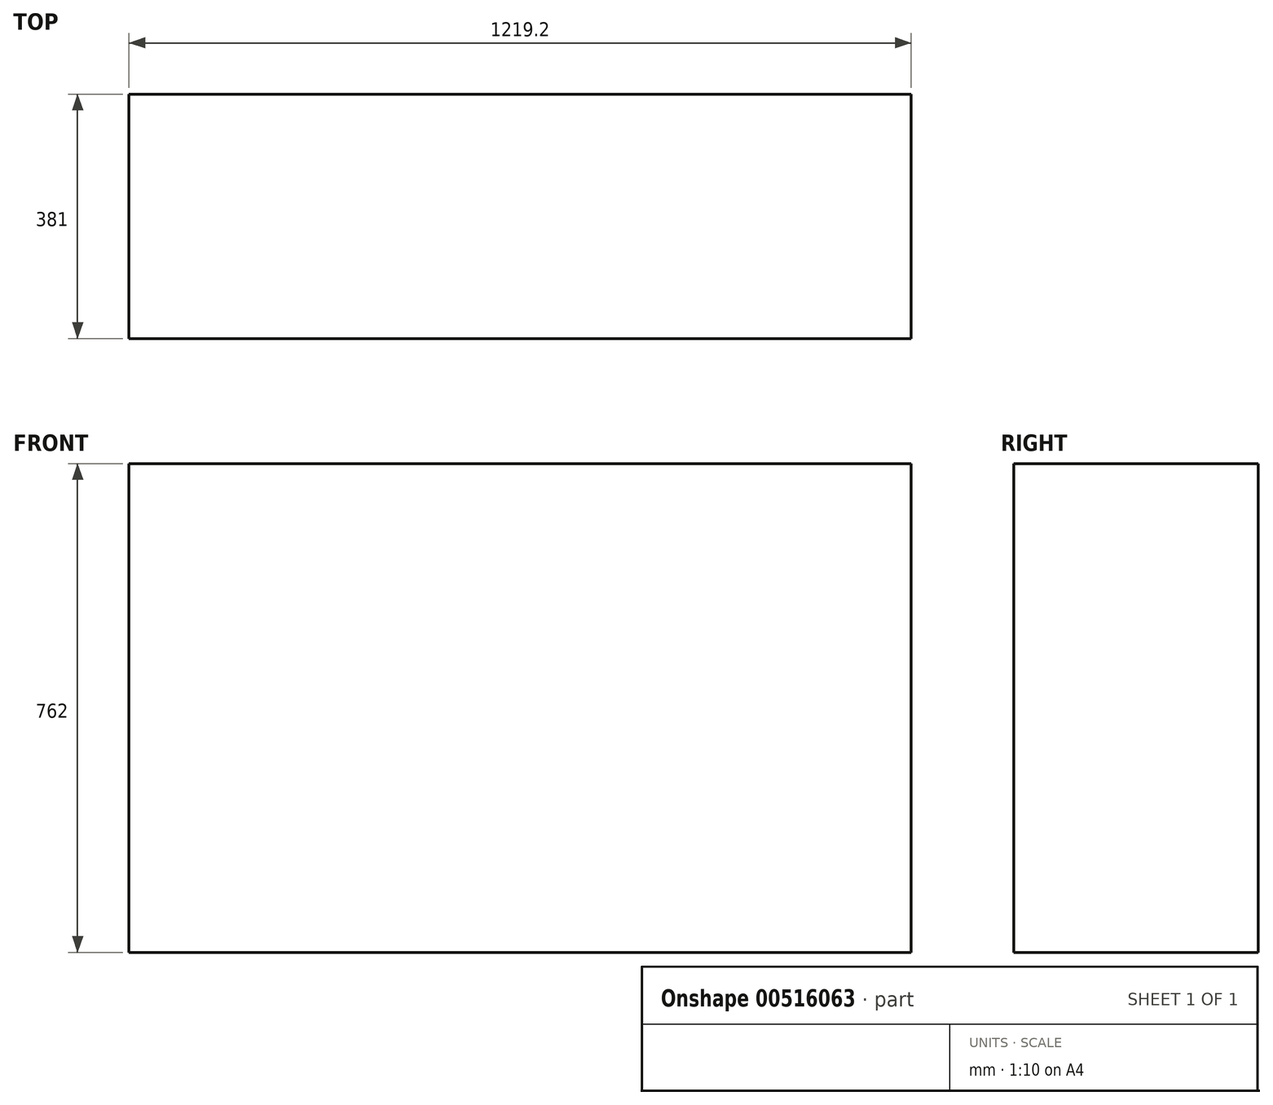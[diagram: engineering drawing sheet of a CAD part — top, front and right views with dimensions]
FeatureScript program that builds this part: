
annotation { "Feature Type Name" : "Feature", "Feature Type Description" : "" }
export const myFeature = defineFeature(function(context is Context, id is Id, definition is map)
    precondition{}
    {
        {
            var Q0;
            Q0=qCreatedBy(makeId("Top.planeOp"),FACE);
            var sketch = newSketch(context, id + "F0", { "sketchPlane" : qUnion([Q0])});
            skLineSegment(sketch, "E0.bottom", {"start": v(609.6, -190.5) * mm, "end": v(-609.6, -190.5) * mm});
            skLineSegment(sketch, "E0.top", {"start": v(609.6, 190.5) * mm, "end": v(-609.6, 190.5) * mm});
            skLineSegment(sketch, "E0.left", {"start": v(609.6, -190.5) * mm, "end": v(609.6, 190.5) * mm});
            skLineSegment(sketch, "E0.right", {"start": v(-609.6, -190.5) * mm, "end": v(-609.6, 190.5) * mm});
            skPoint(sketch, "E0.middle", {"position": v(0, 0) * mm});
            skSolve(sketch);
        }
        {
            var Q0;
            Q0=makeQuery(id+"F0.imprint","IMPRINT",FACE,{"disambiguationData":[TD([[makeQuery(id+"F0.imprint","IMPRINT",EDGE,{"derivedFrom":sQuery(id+"F0.wireOp",EDGE,"E0.bottom")}),-1.0]])]});
            extrude(context, id + "F1", {"entities" : qUnion([Q0]), "depth" : 762 * mm, "offsetDistance" : 25.4 * mm});
        }
    });
